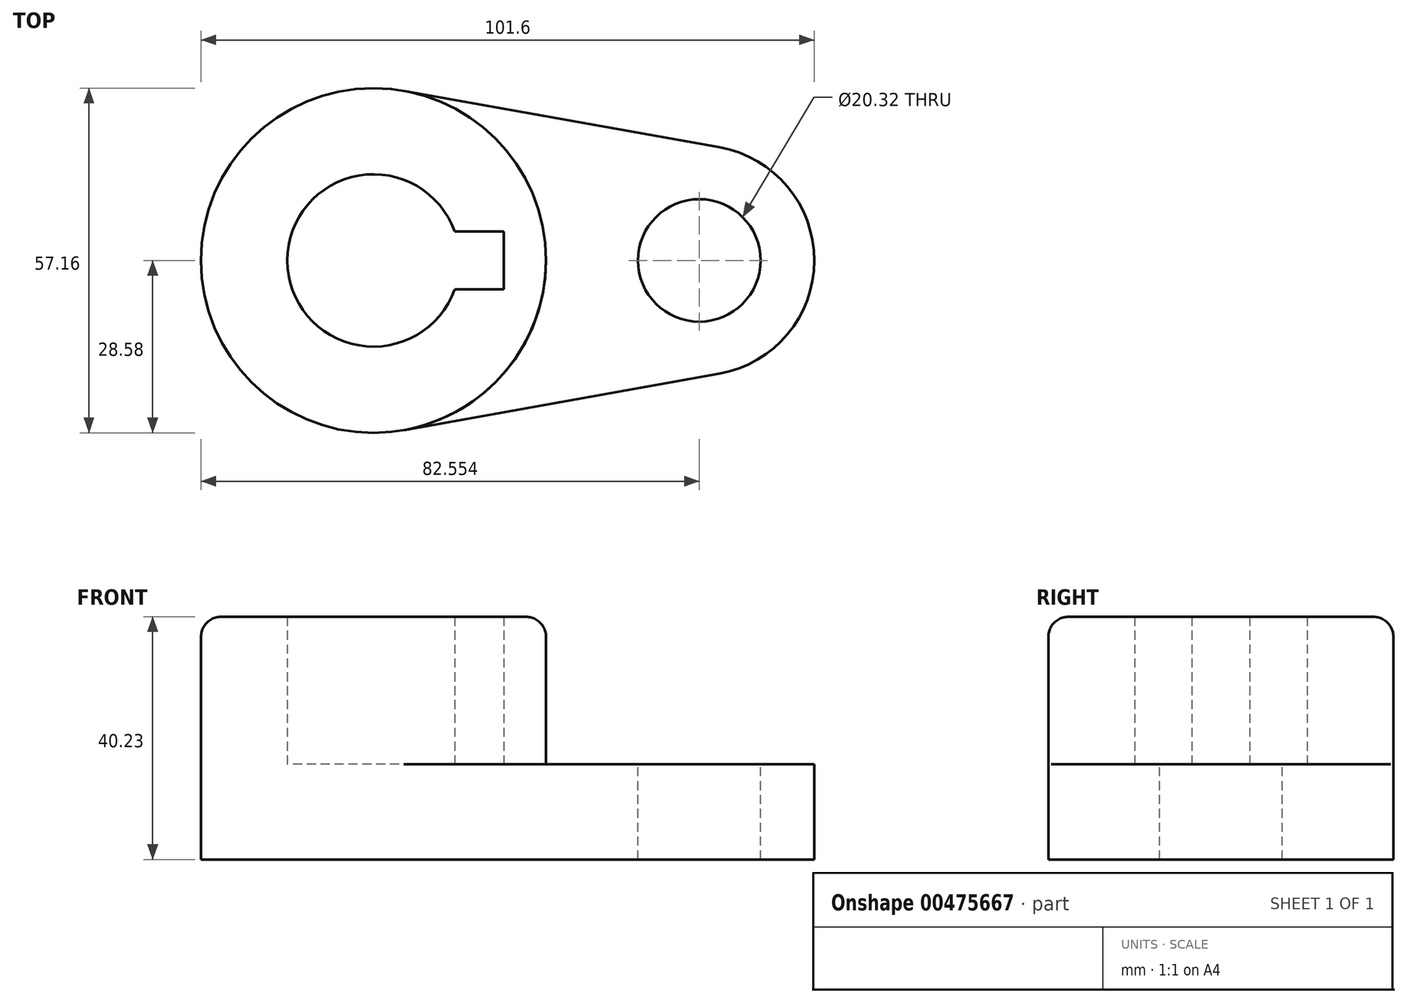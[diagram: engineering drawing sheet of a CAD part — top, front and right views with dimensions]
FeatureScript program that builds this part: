
annotation { "Feature Type Name" : "Feature", "Feature Type Description" : "" }
export const myFeature = defineFeature(function(context is Context, id is Id, definition is map)
    precondition{}
    {
        {
            var Q0;
            Q0=qCreatedBy(makeId("Top.planeOp"),FACE);
            var sketch = newSketch(context, id + "F0", { "sketchPlane" : qUnion([Q0])});
            skCircle(sketch, "E0", {"center": v(-28.24, 0) * mm, "radius": 28.58 * mm});
            skArc(sketch, "E1", {"start": v(-14.78, 4.8) * mm, "mid": v(-42.53, 0) * mm, "end": v(-14.78, -4.8) * mm});
            skCircle(sketch, "E2", {"center": v(25.73, 0) * mm, "radius": 19.05 * mm});
            skCircle(sketch, "E3", {"center": v(25.73, 0) * mm, "radius": 10.16 * mm});
            skLineSegment(sketch, "E4", {"start": v(-23.2, 28.13) * mm, "end": v(29.1, 18.75) * mm});
            skLineSegment(sketch, "E5", {"start": v(-23.2, -28.13) * mm, "end": v(29.1, -18.75) * mm});
            skLineSegment(sketch, "E6", {"start": v(-14.78, 4.8) * mm, "end": v(-6.64, 4.8) * mm});
            skLineSegment(sketch, "E7", {"start": v(-14.78, -4.8) * mm, "end": v(-6.64, -4.8) * mm});
            skLineSegment(sketch, "E8", {"start": v(-6.64, -4.8) * mm, "end": v(-6.64, 4.8) * mm});
            skSolve(sketch);
        }
        {
            var Q0;
            Q0=makeQuery(id+"F0.imprint","IMPRINT",FACE,{"disambiguationData":[TD([[makeQuery(id+"F0.imprint","IMPRINT",EDGE,{"derivedFrom":sQuery(id+"F0.wireOp",EDGE,"E1")}),-1.0]])]});
            var Q1;
            {var subQ0=sQuery(id+"F0.wireOp",EDGE,"E4");Q1=makeQuery(id+"F0.imprint","IMPRINT",FACE,{"disambiguationData":[TD([[makeQuery(id+"F0.imprint","IMPRINT",EDGE,{"derivedFrom":subQ0}),-1.0]])]});}
            var Q2;
            Q2=makeQuery(id+"F0.imprint","IMPRINT",FACE,{"disambiguationData":[TD([[makeQuery(id+"F0.imprint","IMPRINT",EDGE,{"derivedFrom":sQuery(id+"F0.wireOp",EDGE,"E3")}),-1.0]])]});
            var Q3;
            Q3=makeQuery(id+"F0.imprint","IMPRINT",FACE,{"disambiguationData":[TD([[makeQuery(id+"F0.imprint","IMPRINT",EDGE,{"derivedFrom":sQuery(id+"F0.wireOp",EDGE,"E1")}),1.0]])]});
            extrude(context, id + "F1", {"entities" : qUnion([Q0, Q1, Q2, Q3]), "oppositeDirection" : true, "depth" : 15.77 * mm});
        }
        {
            var Q0;
            Q0=makeQuery(id+"F0.imprint","IMPRINT",FACE,{"disambiguationData":[TD([[makeQuery(id+"F0.imprint","IMPRINT",EDGE,{"derivedFrom":sQuery(id+"F0.wireOp",EDGE,"E1")}),-1.0]])]});
            extrude(context, id + "F2", {"entities" : qUnion([Q0]), "operationType" : NewBodyOperationType.ADD, "depth" : 24.46 * mm});
        }
        {
            var Q0;
            Q0=makeQuery(id+"F2.opExtrude","CAP_EDGE",EDGE,{"disambiguationData":[OSD([sQuery(id+"F0.wireOp",EDGE,"E0")])],"isStart":false});
            fillet(context, id + "F3", {"entities" : qUnion([Q0]), "radius" : 3.3 * mm, "tangentPropagation" : true, "allowEdgeOverflow" : false});
        }
    });
